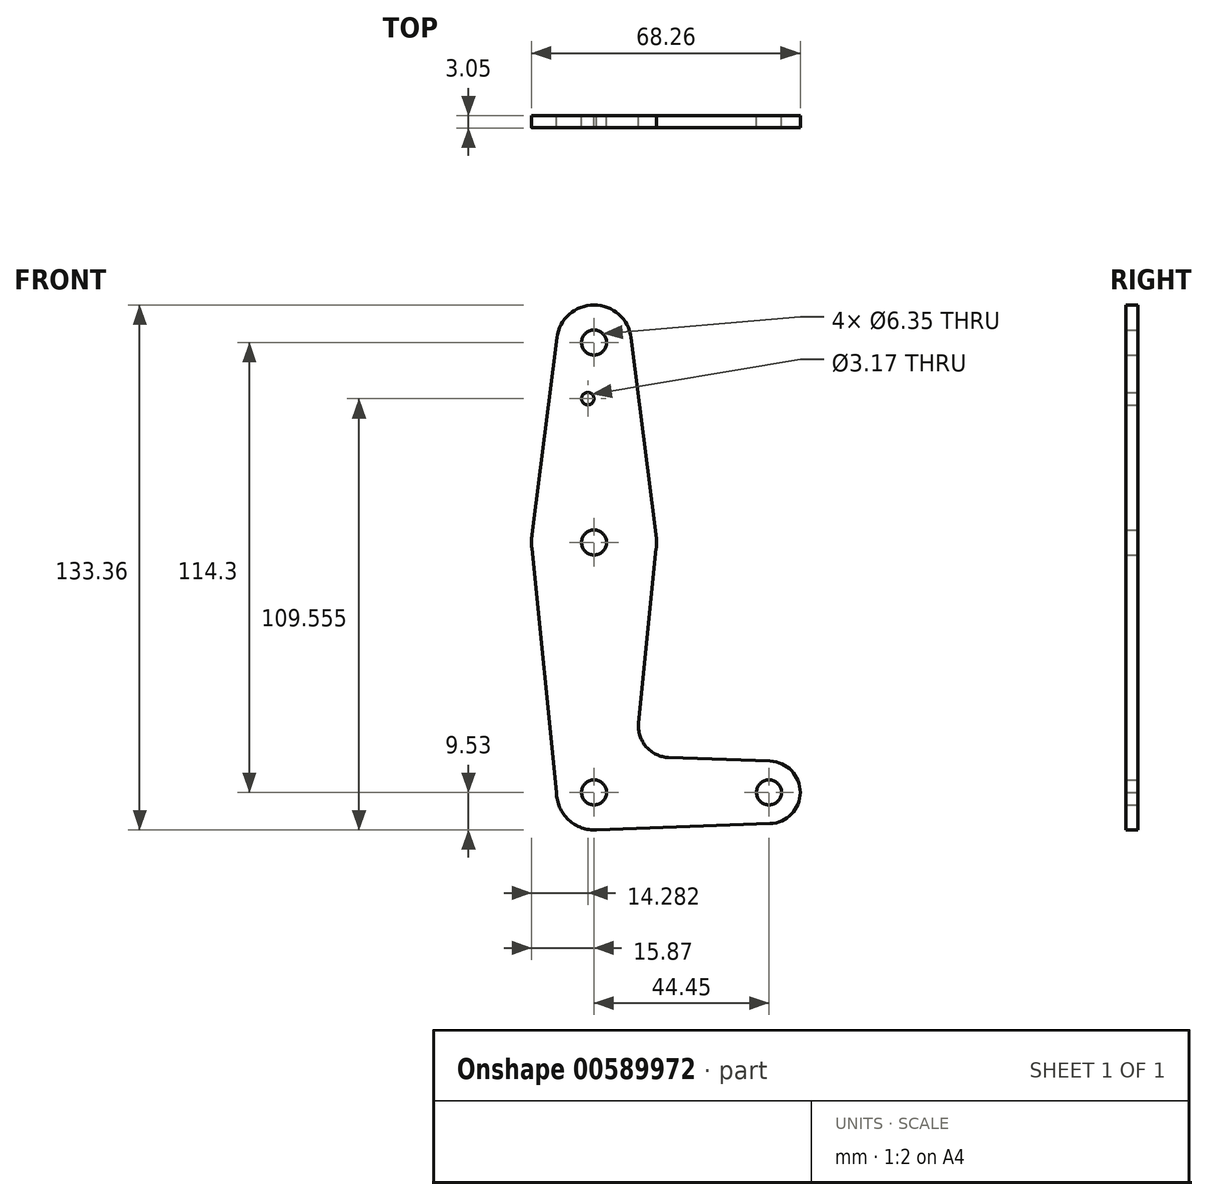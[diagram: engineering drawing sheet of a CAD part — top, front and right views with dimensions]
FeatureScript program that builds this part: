
annotation { "Feature Type Name" : "Feature", "Feature Type Description" : "" }
export const myFeature = defineFeature(function(context is Context, id is Id, definition is map)
    precondition{}
    {
        {
            var Q0;
            Q0=qCreatedBy(makeId("Front.planeOp"),FACE);
            var sketch = newSketch(context, id + "F0", { "sketchPlane" : qUnion([Q0])});
            skLineSegment(sketch, "E0", {"start": v(0, 114.3) * mm, "end": v(0, 0) * mm, "construction": true});
            skLineSegment(sketch, "E1", {"start": v(0, 0) * mm, "end": v(44.45, 0) * mm, "construction": true});
            skCircle(sketch, "E2", {"center": v(0, 114.3) * mm, "radius": 9.53 * mm});
            skCircle(sketch, "E3", {"center": v(0, 63.5) * mm, "radius": 15.88 * mm});
            skCircle(sketch, "E4", {"center": v(0, 0) * mm, "radius": 9.53 * mm});
            skCircle(sketch, "E5", {"center": v(44.45, 0) * mm, "radius": 7.94 * mm});
            skLineSegment(sketch, "E6", {"start": v(-9.52, 0) * mm, "end": v(-15.8, 61.9) * mm});
            skLineSegment(sketch, "E7", {"start": v(0, -9.53) * mm, "end": v(44.73, -7.93) * mm});
            skLineSegment(sketch, "E8", {"start": v(9.45, 115.5) * mm, "end": v(15.75, 65.48) * mm});
            skCircle(sketch, "E9", {"center": v(0, 114.3) * mm, "radius": 3.18 * mm});
            skCircle(sketch, "E10", {"center": v(0, 63.5) * mm, "radius": 3.18 * mm});
            skCircle(sketch, "E11", {"center": v(0, 0) * mm, "radius": 3.18 * mm});
            skCircle(sketch, "E12", {"center": v(44.45, 0) * mm, "radius": 3.18 * mm});
            skCircle(sketch, "E13", {"center": v(-1.59, 100.03) * mm, "radius": 1.59 * mm});
            skLineSegment(sketch, "E14", {"start": v(15.8, 61.91) * mm, "end": v(11.34, 17.6) * mm});
            skLineSegment(sketch, "E15", {"start": v(-9.45, 115.5) * mm, "end": v(-15.75, 65.48) * mm});
            skLineSegment(sketch, "E16", {"start": v(44.73, 7.93) * mm, "end": v(18.97, 8.85) * mm});
            skArc(sketch, "E17.filletArc", {"start": v(11.34, 17.6) * mm, "mid": v(13.26, 11.57) * mm, "end": v(18.97, 8.85) * mm});
            skSolve(sketch);
        }
        {
            var Q0;
            Q0 = qSketchRegion(id + "F0", true);
            extrude(context, id + "F1", {"entities" : qUnion([Q0]), "depth" : 3.05 * mm, "offsetDistance" : 25.4 * mm});
        }
    });
